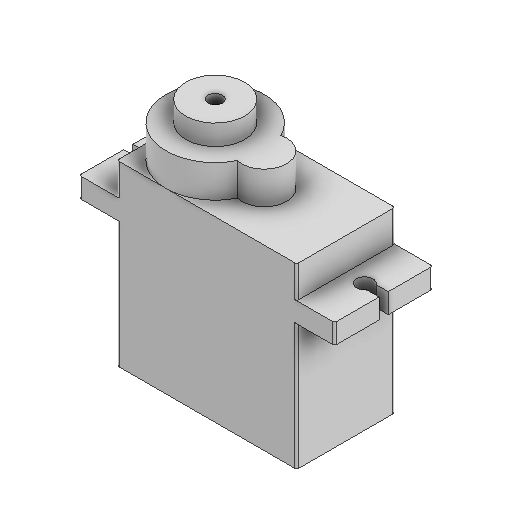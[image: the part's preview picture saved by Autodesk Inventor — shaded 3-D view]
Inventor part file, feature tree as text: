
AUTODESK INVENTOR PART (.ipt)
format: ipt  version: 2025.1 (Build 291241020, 241B)  size: 350,208 bytes
history: native  units: in
note: dims shown in document units (in); Inventor stores cm internally (conversion verified against a paired STEP export)
features: extrude x6, sketch x6, plane x2, projected_geometry x2, mirror x1, fillet x1
ambient origin geometry x8: Origin, YZ Plane, XZ Plane, XY Plane, X Axis, Y Axis, Z Axis, Center Point
bodies: Solid1 (feature_tree)
feature tree (18):
  extrude  "Extrusion1"  Depth=0.875in
  plane  "Work Plane1"
  extrude  "Extrusion2"  [1 undecoded]
  plane  "Work Plane2"
  mirror  "Mirror1"
  extrude  "Extrusion3"  Depth=0.186in
  extrude  "Extrusion4"  Depth=0.22in
  extrude  "Extrusion5"  Depth=0.1in
  fillet  "Fillet1"  Radius=0.1in
  extrude  "Extrusion6"  Depth=0.05in
  sketch  "Sketch1"  dims[d0=0.883in d1=0.875in]
  sketch  "Sketch2"  dims[d2=0.482in d3=0.0in d4=-0.157in]
  sketch  "Sketch3"  dims[d5=0.186in d6=0.08in]
  sketch  "Sketch4"  dims[d7=0.098in d8=0.0in d9=0.22in]
  sketch  "Sketch5"  dims[d10=0.16in d11=0.0in d12=0.289in d13=0.1in d14=0.0in]
  sketch  "Sketch6"  dims[d15=0.07in d16=0.05in d17=0.05in d18=0.05in d19=0.17in d20=0.1in d21=0.0in d22=0.01in d23=0.045in d24=0.0225in d25=0.186in d26=0.1in d27=0.0in]
  projected_geometry  "Projected Loop1"
  projected_geometry  "Projected Loop2"
note: 1 required parameter value undecoded (feature->parameter linkage not recoverable at this tier; creation-order binding heuristic only, values carry confidence <= 0.55)
